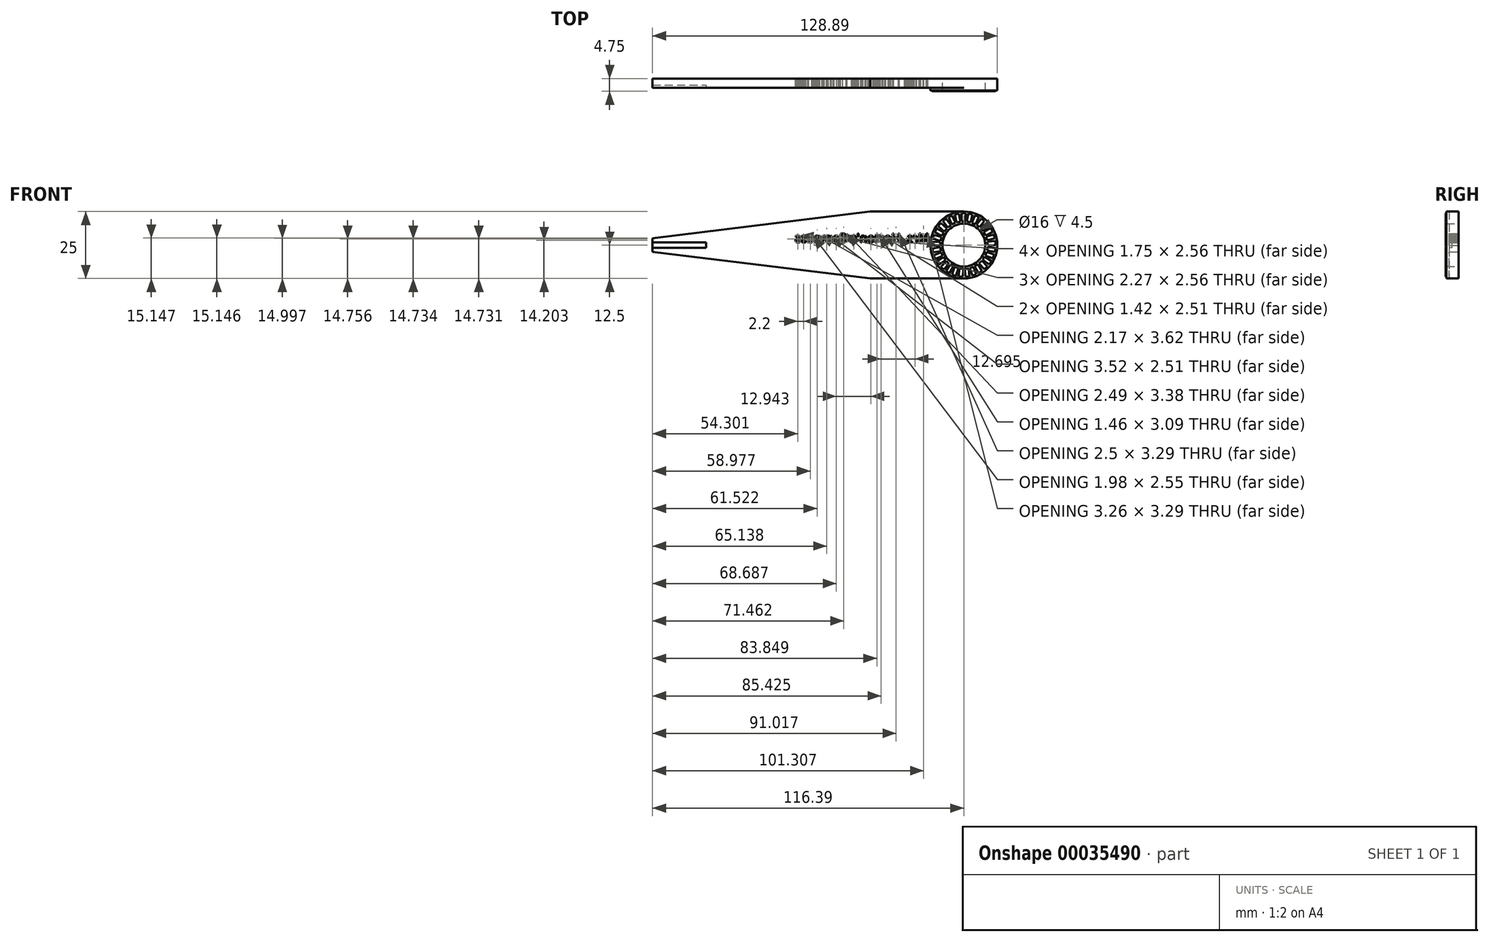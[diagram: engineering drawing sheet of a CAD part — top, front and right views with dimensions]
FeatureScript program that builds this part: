
annotation { "Feature Type Name" : "Feature", "Feature Type Description" : "" }
export const myFeature = defineFeature(function(context is Context, id is Id, definition is map)
    precondition{}
    {
        {
            var Q0;
            Q0=qCreatedBy(makeId("Front.planeOp"),FACE);
            var sketch = newSketch(context, id + "F0", { "sketchPlane" : qUnion([Q0])});
            skCircle(sketch, "E0", {"center": v(0, 0) * mm, "radius": 8 * mm});
            skCircle(sketch, "E1", {"center": v(0, 0) * mm, "radius": 12.5 * mm});
            skLineSegment(sketch, "E2", {"start": v(-35, 12.5) * mm, "end": v(0, 12.5) * mm});
            skLineSegment(sketch, "E3", {"start": v(-35, -12.5) * mm, "end": v(0, -12.5) * mm});
            skLineSegment(sketch, "E4", {"start": v(-136.29, 12.5) * mm, "end": v(-35, 12.5) * mm, "construction": true});
            skLineSegment(sketch, "E5", {"start": v(-35, 12.5) * mm, "end": v(-116.39, 2.5) * mm});
            skLineSegment(sketch, "E6", {"start": v(-35, -12.5) * mm, "end": v(-138.22, -12.5) * mm, "construction": true});
            skLineSegment(sketch, "E7", {"start": v(-35, -12.5) * mm, "end": v(-116.39, -2.5) * mm});
            skLineSegment(sketch, "E8", {"start": v(-116.39, 2.5) * mm, "end": v(-116.39, -2.5) * mm});
            skSolve(sketch);
        }
        {
            var Q0;
            {var subQ1=sQuery(id+"F0.wireOp",EDGE,"E2");Q0=makeQuery(id+"F0.imprint","IMPRINT",FACE,{"disambiguationData":[TD([[makeQuery(id+"F0.imprint","IMPRINT",EDGE,{"derivedFrom":subQ1}),-1.0]])]});}
            var Q1;
            Q1=makeQuery(id+"F0.imprint","IMPRINT",FACE,{"disambiguationData":[TD([[makeQuery(id+"F0.imprint","IMPRINT",EDGE,{"derivedFrom":sQuery(id+"F0.wireOp",EDGE,"E0")}),-1.0]])]});
            extrude(context, id + "F1", {"entities" : qUnion([Q0, Q1]), "depth" : 3.5 * mm});
        }
        {
            var Q0;
            Q0=makeQuery(id+"F1.opExtrude","CAP_FACE",FACE,{"disambiguationData":[OSD([sQuery(id+"F0.wireOp",EDGE,"E0"),sQuery(id+"F0.wireOp",EDGE,"E1"),sQuery(id+"F0.wireOp",EDGE,"E2"),sQuery(id+"F0.wireOp",EDGE,"E3"),sQuery(id+"F0.wireOp",EDGE,"E5"),sQuery(id+"F0.wireOp",EDGE,"E7"),sQuery(id+"F0.wireOp",EDGE,"E8")])],"isStart":false});
            var sketch = newSketch(context, id + "F2", { "sketchPlane" : qUnion([Q0])});
            skCircle(sketch, "E9", {"center": v(0, 0) * mm, "radius": 12.5 * mm});
            skCircle(sketch, "E10", {"center": v(0, 0) * mm, "radius": 8 * mm});
            skLineSegment(sketch, "E11.bottom", {"start": v(-116.39, 1) * mm, "end": v(-96.39, 1) * mm});
            skLineSegment(sketch, "E11.top", {"start": v(-116.39, -1) * mm, "end": v(-96.39, -1) * mm});
            skLineSegment(sketch, "E11.left", {"start": v(-116.39, 1) * mm, "end": v(-116.39, -1) * mm});
            skLineSegment(sketch, "E11.right", {"start": v(-96.39, 1) * mm, "end": v(-96.39, -1) * mm});
            skSolve(sketch);
        }
        {
            var Q0;
            Q0 = qSketchRegion(id + "F2", true);
            extrude(context, id + "F3", {"entities" : qUnion([Q0]), "operationType" : NewBodyOperationType.ADD, "depth" : 1 * mm});
        }
        {
            var Q0;
            Q0=makeQuery(id+"F3.opExtrude","CAP_FACE",FACE,{"disambiguationData":[OSD([sQuery(id+"F2.wireOp",EDGE,"E11.bottom"),sQuery(id+"F2.wireOp",EDGE,"E11.top"),sQuery(id+"F2.wireOp",EDGE,"E11.left"),sQuery(id+"F2.wireOp",EDGE,"E11.right")])],"isStart":false});
            extrude(context, id + "F4", {"entities" : qUnion([Q0]), "operationType" : NewBodyOperationType.REMOVE, "oppositeDirection" : true, "depth" : 2 * mm});
        }
        {
            var Q0;
            Q0=makeQuery(id+"F3.opExtrude","CAP_FACE",FACE,{"disambiguationData":[OSD([sQuery(id+"F2.wireOp",EDGE,"E9"),sQuery(id+"F2.wireOp",EDGE,"E10")])],"isStart":false});
            var sketch = newSketch(context, id + "F5", { "sketchPlane" : qUnion([Q0])});
            skLineSegment(sketch, "E12.bottom", {"start": v(-0.83, 11.87) * mm, "end": v(0.67, 11.87) * mm});
            skLineSegment(sketch, "E12.top", {"start": v(-0.83, 8.87) * mm, "end": v(0.67, 8.87) * mm});
            skLineSegment(sketch, "E12.left", {"start": v(-0.83, 11.87) * mm, "end": v(-0.83, 8.87) * mm});
            skLineSegment(sketch, "E12.right", {"start": v(0.67, 11.87) * mm, "end": v(0.67, 8.87) * mm});
            skLineSegment(sketch, "E13.1.0", {"start": v(1.1, 8.84) * mm, "end": v(2.56, 8.51) * mm});
            skLineSegment(sketch, "E13.1.1", {"start": v(3.2, 11.44) * mm, "end": v(2.56, 8.51) * mm});
            skLineSegment(sketch, "E13.1.2", {"start": v(1.74, 11.77) * mm, "end": v(1.1, 8.84) * mm});
            skLineSegment(sketch, "E13.1.3", {"start": v(1.74, 11.77) * mm, "end": v(3.2, 11.44) * mm});
            skLineSegment(sketch, "E13.2.0", {"start": v(2.97, 8.4) * mm, "end": v(4.33, 7.77) * mm});
            skLineSegment(sketch, "E13.2.1", {"start": v(5.59, 10.49) * mm, "end": v(4.33, 7.77) * mm});
            skLineSegment(sketch, "E13.2.2", {"start": v(4.23, 11.12) * mm, "end": v(2.97, 8.4) * mm});
            skLineSegment(sketch, "E13.2.3", {"start": v(4.23, 11.12) * mm, "end": v(5.59, 10.49) * mm});
            skLineSegment(sketch, "E13.3.0", {"start": v(4.7, 7.56) * mm, "end": v(5.9, 6.65) * mm});
            skLineSegment(sketch, "E13.3.1", {"start": v(7.71, 9.04) * mm, "end": v(5.9, 6.65) * mm});
            skLineSegment(sketch, "E13.3.2", {"start": v(6.52, 9.95) * mm, "end": v(4.7, 7.56) * mm});
            skLineSegment(sketch, "E13.3.3", {"start": v(6.52, 9.95) * mm, "end": v(7.71, 9.04) * mm});
            skLineSegment(sketch, "E13.4.0", {"start": v(6.22, 6.37) * mm, "end": v(7.19, 5.23) * mm});
            skLineSegment(sketch, "E13.4.1", {"start": v(9.48, 7.17) * mm, "end": v(7.19, 5.23) * mm});
            skLineSegment(sketch, "E13.4.2", {"start": v(8.5, 8.32) * mm, "end": v(6.22, 6.37) * mm});
            skLineSegment(sketch, "E13.4.3", {"start": v(8.5, 8.32) * mm, "end": v(9.48, 7.17) * mm});
            skLineSegment(sketch, "E13.5.0", {"start": v(7.44, 4.89) * mm, "end": v(8.15, 3.56) * mm});
            skLineSegment(sketch, "E13.5.1", {"start": v(10.8, 4.97) * mm, "end": v(8.15, 3.56) * mm});
            skLineSegment(sketch, "E13.5.2", {"start": v(10.1, 6.3) * mm, "end": v(7.44, 4.89) * mm});
            skLineSegment(sketch, "E13.5.3", {"start": v(10.1, 6.3) * mm, "end": v(10.8, 4.97) * mm});
            skLineSegment(sketch, "E13.6.0", {"start": v(8.32, 3.17) * mm, "end": v(8.72, 1.73) * mm});
            skLineSegment(sketch, "E13.6.1", {"start": v(11.61, 2.53) * mm, "end": v(8.72, 1.73) * mm});
            skLineSegment(sketch, "E13.6.2", {"start": v(11.21, 3.98) * mm, "end": v(8.32, 3.17) * mm});
            skLineSegment(sketch, "E13.6.3", {"start": v(11.21, 3.98) * mm, "end": v(11.61, 2.53) * mm});
            skLineSegment(sketch, "E13.7.0", {"start": v(8.8, 1.31) * mm, "end": v(8.89, -0.19) * mm});
            skLineSegment(sketch, "E13.7.1", {"start": v(11.88, -0.02) * mm, "end": v(8.89, -0.19) * mm});
            skLineSegment(sketch, "E13.7.2", {"start": v(11.8, 1.47) * mm, "end": v(8.8, 1.31) * mm});
            skLineSegment(sketch, "E13.7.3", {"start": v(11.8, 1.47) * mm, "end": v(11.88, -0.02) * mm});
            skLineSegment(sketch, "E13.8.0", {"start": v(8.88, -0.61) * mm, "end": v(8.64, -2.1) * mm});
            skLineSegment(sketch, "E13.8.1", {"start": v(11.6, -2.58) * mm, "end": v(8.64, -2.1) * mm});
            skLineSegment(sketch, "E13.8.2", {"start": v(11.84, -1.1) * mm, "end": v(8.88, -0.61) * mm});
            skLineSegment(sketch, "E13.8.3", {"start": v(11.84, -1.1) * mm, "end": v(11.6, -2.58) * mm});
            skLineSegment(sketch, "E13.9.0", {"start": v(8.54, -2.5) * mm, "end": v(7.99, -3.9) * mm});
            skLineSegment(sketch, "E13.9.1", {"start": v(10.78, -5.01) * mm, "end": v(7.99, -3.9) * mm});
            skLineSegment(sketch, "E13.9.2", {"start": v(11.33, -3.62) * mm, "end": v(8.54, -2.5) * mm});
            skLineSegment(sketch, "E13.9.3", {"start": v(11.33, -3.62) * mm, "end": v(10.78, -5.01) * mm});
            skLineSegment(sketch, "E13.10.0", {"start": v(7.8, -4.29) * mm, "end": v(6.96, -5.53) * mm});
            skLineSegment(sketch, "E13.10.1", {"start": v(9.45, -7.21) * mm, "end": v(6.96, -5.53) * mm});
            skLineSegment(sketch, "E13.10.2", {"start": v(10.29, -5.97) * mm, "end": v(7.8, -4.29) * mm});
            skLineSegment(sketch, "E13.10.3", {"start": v(10.29, -5.97) * mm, "end": v(9.45, -7.21) * mm});
            skLineSegment(sketch, "E13.11.0", {"start": v(6.7, -5.86) * mm, "end": v(5.61, -6.9) * mm});
            skLineSegment(sketch, "E13.11.1", {"start": v(7.68, -9.07) * mm, "end": v(5.61, -6.9) * mm});
            skLineSegment(sketch, "E13.11.2", {"start": v(8.76, -8.04) * mm, "end": v(6.7, -5.86) * mm});
            skLineSegment(sketch, "E13.11.3", {"start": v(8.76, -8.04) * mm, "end": v(7.68, -9.07) * mm});
            skLineSegment(sketch, "E13.12.0", {"start": v(5.28, -7.17) * mm, "end": v(4, -7.94) * mm});
            skLineSegment(sketch, "E13.12.1", {"start": v(5.55, -10.51) * mm, "end": v(4, -7.94) * mm});
            skLineSegment(sketch, "E13.12.2", {"start": v(6.83, -9.74) * mm, "end": v(5.28, -7.17) * mm});
            skLineSegment(sketch, "E13.12.3", {"start": v(6.83, -9.74) * mm, "end": v(5.55, -10.51) * mm});
            skLineSegment(sketch, "E13.13.0", {"start": v(3.62, -8.14) * mm, "end": v(2.2, -8.61) * mm});
            skLineSegment(sketch, "E13.13.1", {"start": v(3.16, -11.46) * mm, "end": v(2.2, -8.61) * mm});
            skLineSegment(sketch, "E13.13.2", {"start": v(4.58, -10.98) * mm, "end": v(3.62, -8.14) * mm});
            skLineSegment(sketch, "E13.13.3", {"start": v(4.58, -10.98) * mm, "end": v(3.16, -11.46) * mm});
            skLineSegment(sketch, "E13.14.0", {"start": v(1.79, -8.72) * mm, "end": v(0.3, -8.89) * mm});
            skLineSegment(sketch, "E13.14.1", {"start": v(0.62, -11.87) * mm, "end": v(0.3, -8.89) * mm});
            skLineSegment(sketch, "E13.14.2", {"start": v(2.11, -11.7) * mm, "end": v(1.79, -8.72) * mm});
            skLineSegment(sketch, "E13.14.3", {"start": v(2.11, -11.7) * mm, "end": v(0.62, -11.87) * mm});
            skLineSegment(sketch, "E13.15.0", {"start": v(-0.13, -8.9) * mm, "end": v(-1.62, -8.74) * mm});
            skLineSegment(sketch, "E13.15.1", {"start": v(-1.95, -11.72) * mm, "end": v(-1.62, -8.74) * mm});
            skLineSegment(sketch, "E13.15.2", {"start": v(-0.46, -11.89) * mm, "end": v(-0.13, -8.9) * mm});
            skLineSegment(sketch, "E13.15.3", {"start": v(-0.46, -11.89) * mm, "end": v(-1.95, -11.72) * mm});
            skLineSegment(sketch, "E13.16.0", {"start": v(-2.04, -8.67) * mm, "end": v(-3.46, -8.19) * mm});
            skLineSegment(sketch, "E13.16.1", {"start": v(-4.42, -11.03) * mm, "end": v(-3.46, -8.19) * mm});
            skLineSegment(sketch, "E13.16.2", {"start": v(-3, -11.51) * mm, "end": v(-2.04, -8.67) * mm});
            skLineSegment(sketch, "E13.16.3", {"start": v(-3, -11.51) * mm, "end": v(-4.42, -11.03) * mm});
            skLineSegment(sketch, "E13.17.0", {"start": v(-3.86, -8.03) * mm, "end": v(-5.14, -7.25) * mm});
            skLineSegment(sketch, "E13.17.1", {"start": v(-6.69, -9.82) * mm, "end": v(-5.14, -7.25) * mm});
            skLineSegment(sketch, "E13.17.2", {"start": v(-5.4, -10.6) * mm, "end": v(-3.86, -8.03) * mm});
            skLineSegment(sketch, "E13.17.3", {"start": v(-5.4, -10.6) * mm, "end": v(-6.69, -9.82) * mm});
            skLineSegment(sketch, "E13.18.0", {"start": v(-5.5, -7) * mm, "end": v(-6.58, -5.98) * mm});
            skLineSegment(sketch, "E13.18.1", {"start": v(-8.65, -8.16) * mm, "end": v(-6.58, -5.98) * mm});
            skLineSegment(sketch, "E13.18.2", {"start": v(-7.56, -9.19) * mm, "end": v(-5.5, -7) * mm});
            skLineSegment(sketch, "E13.18.3", {"start": v(-7.56, -9.19) * mm, "end": v(-8.65, -8.16) * mm});
            skLineSegment(sketch, "E13.19.0", {"start": v(-6.87, -5.66) * mm, "end": v(-7.71, -4.42) * mm});
            skLineSegment(sketch, "E13.19.1", {"start": v(-10.2, -6.1) * mm, "end": v(-7.71, -4.42) * mm});
            skLineSegment(sketch, "E13.19.2", {"start": v(-9.35, -7.35) * mm, "end": v(-6.87, -5.66) * mm});
            skLineSegment(sketch, "E13.19.3", {"start": v(-9.35, -7.35) * mm, "end": v(-10.2, -6.1) * mm});
            skLineSegment(sketch, "E13.20.0", {"start": v(-7.93, -4.05) * mm, "end": v(-8.48, -2.66) * mm});
            skLineSegment(sketch, "E13.20.1", {"start": v(-11.27, -3.77) * mm, "end": v(-8.48, -2.66) * mm});
            skLineSegment(sketch, "E13.20.2", {"start": v(-10.72, -5.16) * mm, "end": v(-7.93, -4.05) * mm});
            skLineSegment(sketch, "E13.20.3", {"start": v(-10.72, -5.16) * mm, "end": v(-11.27, -3.77) * mm});
            skLineSegment(sketch, "E13.21.0", {"start": v(-8.61, -2.26) * mm, "end": v(-8.86, -0.78) * mm});
            skLineSegment(sketch, "E13.21.1", {"start": v(-11.82, -1.26) * mm, "end": v(-8.86, -0.78) * mm});
            skLineSegment(sketch, "E13.21.2", {"start": v(-11.57, -2.74) * mm, "end": v(-8.61, -2.26) * mm});
            skLineSegment(sketch, "E13.21.3", {"start": v(-11.57, -2.74) * mm, "end": v(-11.82, -1.26) * mm});
            skLineSegment(sketch, "E13.22.0", {"start": v(-8.9, -0.35) * mm, "end": v(-8.82, 1.15) * mm});
            skLineSegment(sketch, "E13.22.1", {"start": v(-11.81, 1.3) * mm, "end": v(-8.82, 1.15) * mm});
            skLineSegment(sketch, "E13.22.2", {"start": v(-11.9, -0.19) * mm, "end": v(-8.9, -0.35) * mm});
            skLineSegment(sketch, "E13.22.3", {"start": v(-11.9, -0.19) * mm, "end": v(-11.81, 1.3) * mm});
            skLineSegment(sketch, "E13.23.0", {"start": v(-8.77, 1.57) * mm, "end": v(-8.36, 3.02) * mm});
            skLineSegment(sketch, "E13.23.1", {"start": v(-11.25, 3.82) * mm, "end": v(-8.36, 3.02) * mm});
            skLineSegment(sketch, "E13.23.2", {"start": v(-11.66, 2.37) * mm, "end": v(-8.77, 1.57) * mm});
            skLineSegment(sketch, "E13.23.3", {"start": v(-11.66, 2.37) * mm, "end": v(-11.25, 3.82) * mm});
            skLineSegment(sketch, "E13.24.0", {"start": v(-8.22, 3.42) * mm, "end": v(-7.52, 4.74) * mm});
            skLineSegment(sketch, "E13.24.1", {"start": v(-10.17, 6.15) * mm, "end": v(-7.52, 4.74) * mm});
            skLineSegment(sketch, "E13.24.2", {"start": v(-10.87, 4.82) * mm, "end": v(-8.22, 3.42) * mm});
            skLineSegment(sketch, "E13.24.3", {"start": v(-10.87, 4.82) * mm, "end": v(-10.17, 6.15) * mm});
            skLineSegment(sketch, "E13.25.0", {"start": v(-7.3, 5.1) * mm, "end": v(-6.32, 6.25) * mm});
            skLineSegment(sketch, "E13.25.1", {"start": v(-8.61, 8.2) * mm, "end": v(-6.32, 6.25) * mm});
            skLineSegment(sketch, "E13.25.2", {"start": v(-9.58, 7.05) * mm, "end": v(-7.3, 5.1) * mm});
            skLineSegment(sketch, "E13.25.3", {"start": v(-9.58, 7.05) * mm, "end": v(-8.61, 8.2) * mm});
            skLineSegment(sketch, "E13.26.0", {"start": v(-6.03, 6.55) * mm, "end": v(-4.83, 7.46) * mm});
            skLineSegment(sketch, "E13.26.1", {"start": v(-6.65, 9.85) * mm, "end": v(-4.83, 7.46) * mm});
            skLineSegment(sketch, "E13.26.2", {"start": v(-7.84, 8.94) * mm, "end": v(-6.03, 6.55) * mm});
            skLineSegment(sketch, "E13.26.3", {"start": v(-7.84, 8.94) * mm, "end": v(-6.65, 9.85) * mm});
            skLineSegment(sketch, "E13.27.0", {"start": v(-4.48, 7.7) * mm, "end": v(-3.12, 8.33) * mm});
            skLineSegment(sketch, "E13.27.1", {"start": v(-4.38, 11.05) * mm, "end": v(-3.12, 8.33) * mm});
            skLineSegment(sketch, "E13.27.2", {"start": v(-5.74, 10.42) * mm, "end": v(-4.48, 7.7) * mm});
            skLineSegment(sketch, "E13.27.3", {"start": v(-5.74, 10.42) * mm, "end": v(-4.38, 11.05) * mm});
            skLineSegment(sketch, "E13.28.0", {"start": v(-2.72, 8.48) * mm, "end": v(-1.25, 8.8) * mm});
            skLineSegment(sketch, "E13.28.1", {"start": v(-1.9, 11.73) * mm, "end": v(-1.25, 8.8) * mm});
            skLineSegment(sketch, "E13.28.2", {"start": v(-3.36, 11.4) * mm, "end": v(-2.72, 8.48) * mm});
            skLineSegment(sketch, "E13.28.3", {"start": v(-3.36, 11.4) * mm, "end": v(-1.9, 11.73) * mm});
            skPoint(sketch, "E13.center", {"position": v(0, 0) * mm});
            skLineSegment(sketch, "E13.anchor1", {"start": v(0, 0) * mm, "end": v(-0.83, 8.87) * mm, "construction": true});
            skSolve(sketch);
        }
        {
            var Q0;
            Q0 = qSketchRegion(id + "F5", true);
            extrude(context, id + "F6", {"entities" : qUnion([Q0]), "operationType" : NewBodyOperationType.ADD, "depth" : .25 * mm});
        }
        {
            var Q0;
            Q0=makeQuery(id+"F1.opExtrude","CAP_FACE",FACE,{"disambiguationData":[OSD([sQuery(id+"F0.wireOp",EDGE,"E0"),sQuery(id+"F0.wireOp",EDGE,"E1"),sQuery(id+"F0.wireOp",EDGE,"E2"),sQuery(id+"F0.wireOp",EDGE,"E3"),sQuery(id+"F0.wireOp",EDGE,"E5"),sQuery(id+"F0.wireOp",EDGE,"E7"),sQuery(id+"F0.wireOp",EDGE,"E8")])],"isStart":true});
            var sketch = newSketch(context, id + "F7", { "sketchPlane" : qUnion([Q0])});
            skText(sketch, "E14", { "text": "Mrs. Horton\'s Compass", "fontName": "OpenSans-Regular.ttf"});
            const initialGuessF7  = {"E14": [0.013, 0.001, 1, 0, 0.00332]};
            skSetInitialGuess(sketch, initialGuessF7);
            skSolve(sketch);
        }
        {
            var Q0;
            Q0 = qSketchRegion(id + "F7", true);
            extrude(context, id + "F8", {"entities" : qUnion([Q0]), "operationType" : NewBodyOperationType.REMOVE, "endBound" : BoundingType.THROUGH_ALL, "oppositeDirection" : true, "depth" : 25 * mm});
        }
    });
